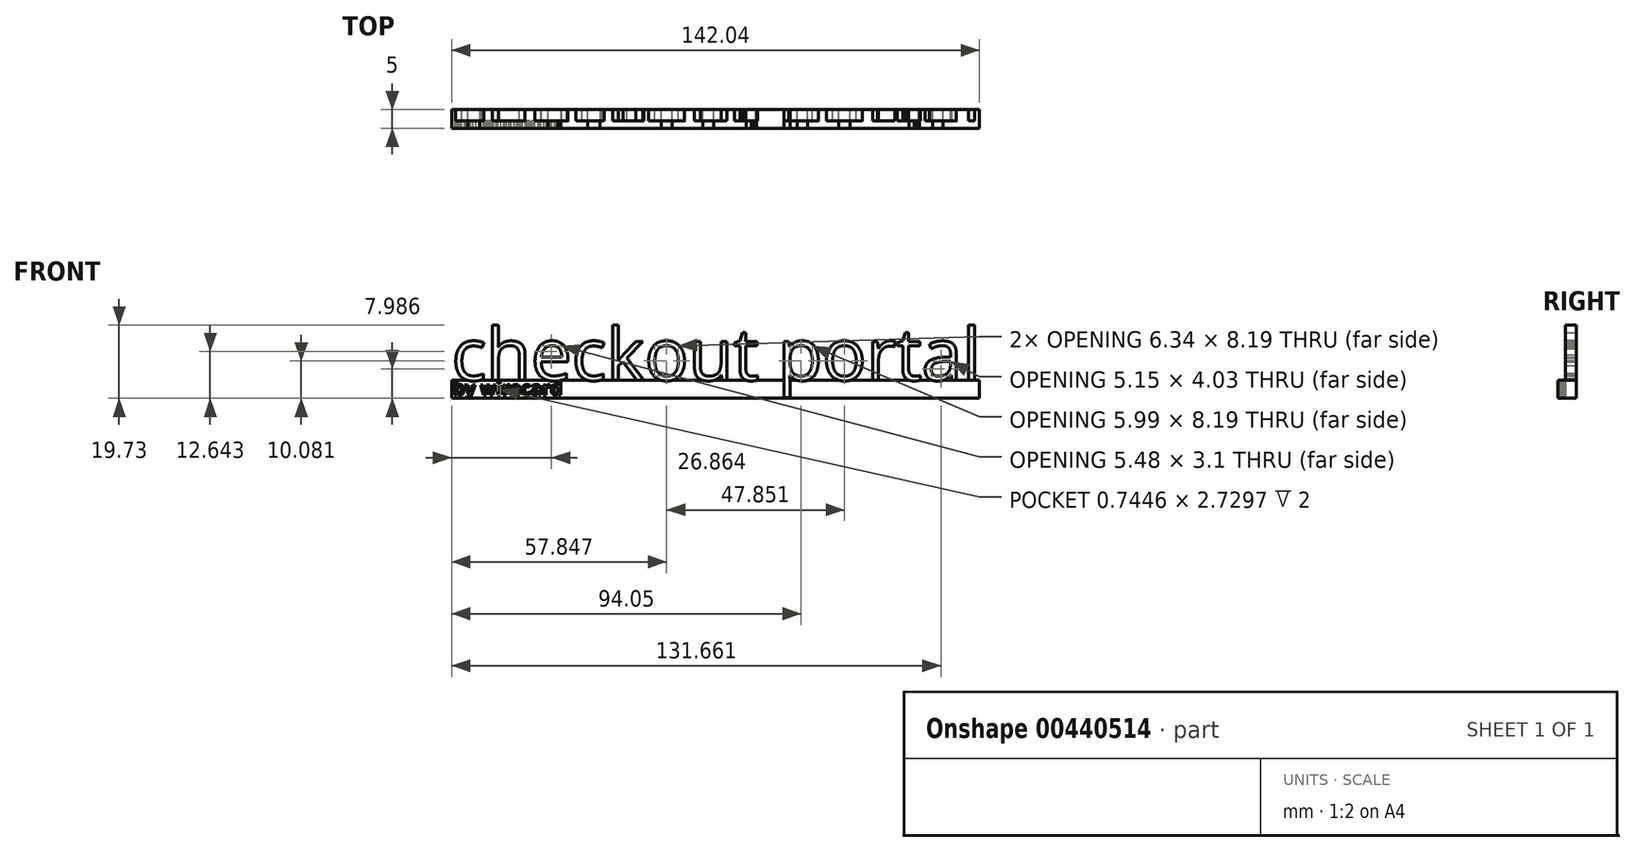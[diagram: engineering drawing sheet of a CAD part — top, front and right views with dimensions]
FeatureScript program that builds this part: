
annotation { "Feature Type Name" : "Feature", "Feature Type Description" : "" }
export const myFeature = defineFeature(function(context is Context, id is Id, definition is map)
    precondition{}
    {
        {
            var Q0;
            Q0=qCreatedBy(makeId("Front.planeOp"),FACE);
            var sketch = newSketch(context, id + "F0", { "sketchPlane" : qUnion([Q0])});
            skText(sketch, "E0", { "text": "checkout portal", "fontName": "OpenSans-Regular.ttf"});
            skLineSegment(sketch, "E1.bottom", {"start": v(-71.48, 0) * mm, "end": v(70.56, 0) * mm});
            skLineSegment(sketch, "E1.top", {"start": v(-71.48, -4.85) * mm, "end": v(70.56, -4.85) * mm});
            skLineSegment(sketch, "E1.left", {"start": v(-71.48, 0) * mm, "end": v(-71.48, -4.85) * mm});
            skLineSegment(sketch, "E1.right", {"start": v(70.56, 0) * mm, "end": v(70.56, -4.85) * mm});
            const initialGuessF0  = {"E0": [-0.07148, 0, 1, 0, 0.0141]};
            skSetInitialGuess(sketch, initialGuessF0);
            skSolve(sketch);
        }
        {
            var Q0;
            Q0 = qSketchRegion(id + "F0", true);
            extrude(context, id + "F1", {"entities" : qUnion([Q0]), "depth" : 3 * mm});
        }
        {
            var Q0;
            {var subQ51=sQuery(id+"F0.wireOp",EDGE,"E0.sketch_text.stroke-46");Q0=makeQuery(id+"F0.imprint","IMPRINT",FACE,{"disambiguationData":[TD([[makeQuery(id+"F0.imprint","IMPRINT",EDGE,{"derivedFrom":subQ51}),1.0]])]});}
            extrude(context, id + "F2", {"entities" : qUnion([Q0]), "operationType" : NewBodyOperationType.ADD, "depth" : 5 * mm});
        }
        {
            var Q0;
            Q0=makeQuery(id+"F2.opExtrude","CAP_FACE",FACE,{"disambiguationData":[OSD([sQuery(id+"F0.wireOp",EDGE,"E0.sketch_text.stroke-0"),sQuery(id+"F0.wireOp",EDGE,"E0.sketch_text.stroke-14"),sQuery(id+"F0.wireOp",EDGE,"E0.sketch_text.stroke-33"),sQuery(id+"F0.wireOp",EDGE,"E0.sketch_text.stroke-45"),sQuery(id+"F0.wireOp",EDGE,"E0.sketch_text.stroke-46"),sQuery(id+"F0.wireOp",EDGE,"E0.sketch_text.stroke-52"),sQuery(id+"F0.wireOp",EDGE,"E0.sketch_text.stroke-66"),sQuery(id+"F0.wireOp",EDGE,"E0.sketch_text.stroke-83"),sQuery(id+"F0.wireOp",EDGE,"E0.sketch_text.stroke-84"),sQuery(id+"F0.wireOp",EDGE,"E0.sketch_text.stroke-111"),sQuery(id+"F0.wireOp",EDGE,"E0.sketch_text.stroke-112"),sQuery(id+"F0.wireOp",EDGE,"E0.sketch_text.stroke-119"),sQuery(id+"F0.wireOp",EDGE,"E0.sketch_text.stroke-120"),sQuery(id+"F0.wireOp",EDGE,"E0.sketch_text.stroke-121"),sQuery(id+"F0.wireOp",EDGE,"E0.sketch_text.stroke-135"),sQuery(id+"F0.wireOp",EDGE,"E0.sketch_text.stroke-138"),sQuery(id+"F0.wireOp",EDGE,"E0.sketch_text.stroke-139"),sQuery(id+"F0.wireOp",EDGE,"E0.sketch_text.stroke-140"),sQuery(id+"F0.wireOp",EDGE,"E0.sketch_text.stroke-141"),sQuery(id+"F0.wireOp",EDGE,"E0.sketch_text.stroke-150"),sQuery(id+"F0.wireOp",EDGE,"E0.sketch_text.stroke-161"),sQuery(id+"F0.wireOp",EDGE,"E0.sketch_text.stroke-162"),sQuery(id+"F0.wireOp",EDGE,"E0.sketch_text.stroke-193"),sQuery(id+"F0.wireOp",EDGE,"E0.sketch_text.stroke-194"),sQuery(id+"F0.wireOp",EDGE,"E0.sketch_text.stroke-195"),sQuery(id+"F0.wireOp",EDGE,"E0.sketch_text.stroke-212"),sQuery(id+"F0.wireOp",EDGE,"E0.sketch_text.stroke-213"),sQuery(id+"F0.wireOp",EDGE,"E1.bottom"),sQuery(id+"F0.wireOp",EDGE,"E1.top"),sQuery(id+"F0.wireOp",EDGE,"E1.left"),sQuery(id+"F0.wireOp",EDGE,"E1.right")])],"isStart":false});
            var sketch = newSketch(context, id + "F3", { "sketchPlane" : qUnion([Q0])});
            skText(sketch, "E2", { "text": "by wirecard", "fontName": "OpenSans-Bold.ttf"});
            const initialGuessF3  = {"E2": [-0.07112, -0.00391, 1, 0, 0.0036]};
            skSetInitialGuess(sketch, initialGuessF3);
            skSolve(sketch);
        }
        {
            var Q0;
            Q0 = qSketchRegion(id + "F3", true);
            extrude(context, id + "F4", {"entities" : qUnion([Q0]), "operationType" : NewBodyOperationType.REMOVE, "oppositeDirection" : true, "depth" : 2 * mm});
        }
    });
